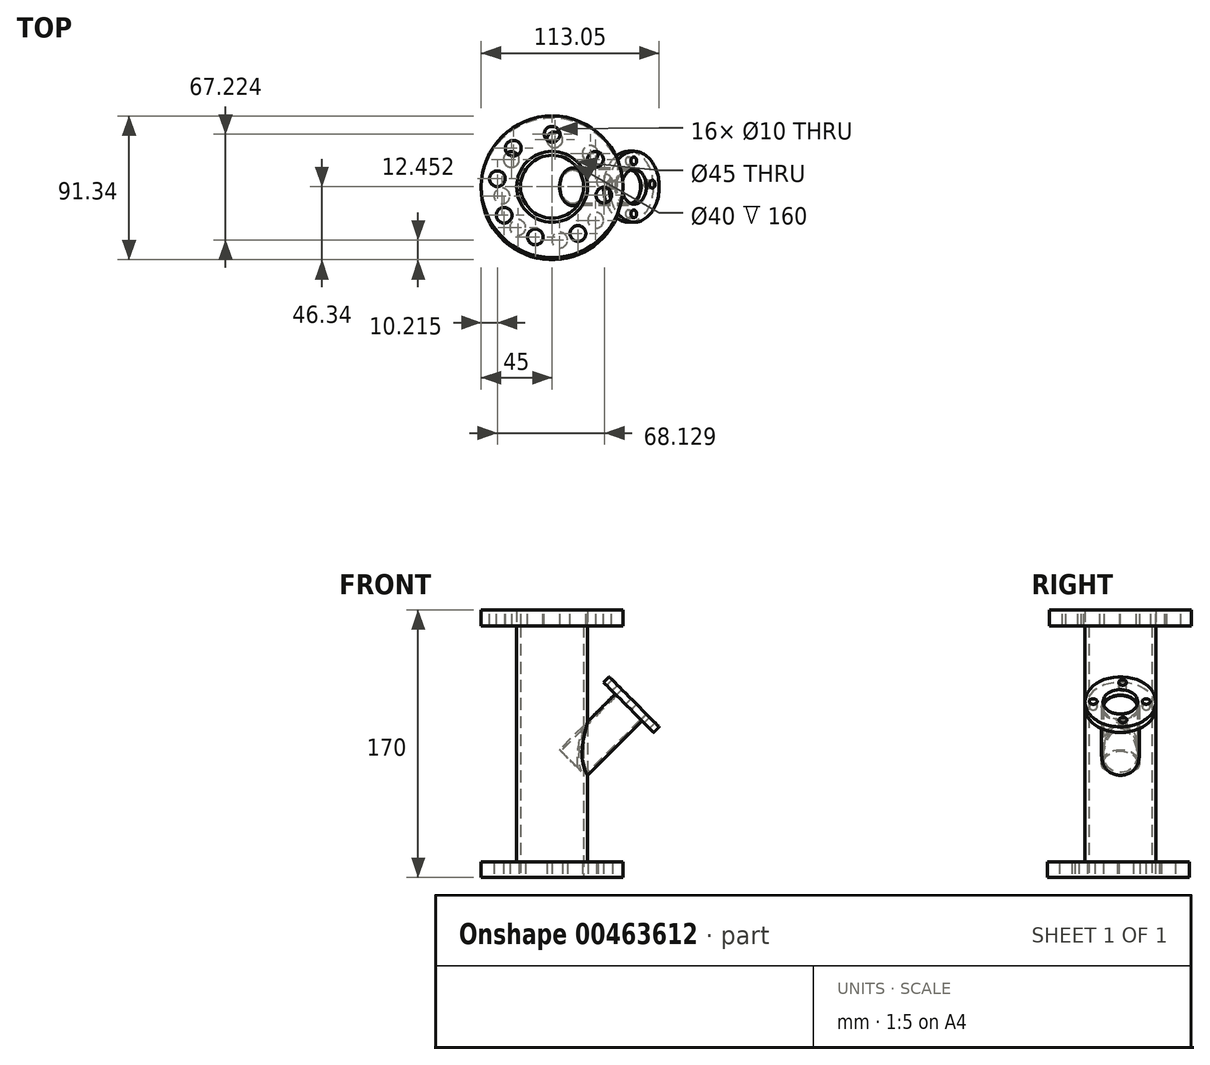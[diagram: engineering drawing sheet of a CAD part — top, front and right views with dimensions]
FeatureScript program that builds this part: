
annotation { "Feature Type Name" : "Feature", "Feature Type Description" : "" }
export const myFeature = defineFeature(function(context is Context, id is Id, definition is map)
    precondition{}
    {
        {
            var Q0;
            Q0=qCreatedBy(makeId("Top.planeOp"),FACE);
            var sketch = newSketch(context, id + "F0", { "sketchPlane" : qUnion([Q0])});
            skCircle(sketch, "E0", {"center": v(0, 0) * mm, "radius": 20 * mm});
            skCircle(sketch, "E1", {"center": v(0, 0) * mm, "radius": 22.5 * mm});
            skSolve(sketch);
        }
        {
            var Q0;
            Q0 = qSketchRegion(id + "F0", true);
            var Q1;
            Q1 = qSketchRegion(id + "F2", true);
            extrude(context, id + "F1", {"entities" : qUnion([Q0, Q1]), "depth" : 160 * mm});
        }
        {
            var Q0;
            Q0=qCreatedBy(makeId("Top.planeOp"),FACE);
            var sketch = newSketch(context, id + "F2", { "sketchPlane" : qUnion([Q0])});
            skCircle(sketch, "E2", {"center": v(0, -1.34) * mm, "radius": 45 * mm});
            skCircle(sketch, "E3", {"center": v(0, 0) * mm, "radius": 22.5 * mm});
            skSolve(sketch);
        }
        {
            var Q0;
            Q0=makeQuery(id+"F1.opExtrude","CAP_FACE",FACE,{"disambiguationData":[OSD([sQuery(id+"F0.wireOp",EDGE,"E0"),sQuery(id+"F0.wireOp",EDGE,"E1")])],"isStart":false});
            var sketch = newSketch(context, id + "F3", { "sketchPlane" : qUnion([Q0])});
            skCircle(sketch, "E4", {"center": v(0, 0) * mm, "radius": 45 * mm});
            skCircle(sketch, "E5", {"center": v(0, 0) * mm, "radius": 35 * mm, "construction": true});
            skSolve(sketch);
        }
        {
            var Q0;
            Q0=makeQuery(id+"F3.imprint","IMPRINT",FACE,{"disambiguationData":[TD([[makeQuery(id+"F3.imprint","IMPRINT",EDGE,{"derivedFrom":sQuery(id+"F3.wireOp",EDGE,"E4")}),1.0]])]});
            var Q1;
            Q1=sQuery(id+"F3.wireOp",EDGE,"E5");
            extrude(context, id + "F4", {"entities" : qUnion([Q0]), "surfaceEntities" : qUnion([Q1]), "depth" : 10 * mm});
        }
        {
            var Q0;
            Q0 = qSketchRegion(id + "F2", true);
            extrude(context, id + "F5", {"entities" : qUnion([Q0]), "operationType" : NewBodyOperationType.ADD, "depth" : 10 * mm});
        }
        {
            var Q0;
            Q0=qCreatedBy(makeId("Front.planeOp"),FACE);
            var sketch = newSketch(context, id + "F6", { "sketchPlane" : qUnion([Q0])});
            skLineSegment(sketch, "E6", {"start": v(0, 0) * mm, "end": v(0, 40) * mm});
            skLineSegment(sketch, "E7", {"start": v(0, 40) * mm, "end": v(23, 63) * mm});
            skLineSegment(sketch, "E8", {"start": v(23, 63) * mm, "end": v(3.42, 82.59) * mm});
            skSolve(sketch);
        }
        {
            var Q0;
            Q0=qCreatedBy(makeId("Right.planeOp"),FACE);
            var Q1;
            Q1=sQuery(id+"F6.wireOp",EDGE,"E8");
            cPlane(context, id + "F7", {"entities" : qUnion([Q0, Q1]), "cplaneType" : CPlaneType.LINE_ANGLE, "offset" : 25 * mm, "angle" : 0 * degree, "width" : 150 * mm, "height" : 150 * mm});
        }
        {
            var Q0;
            Q0=qCreatedBy(id+"F7.planeOp",FACE);
            var sketch = newSketch(context, id + "F8", { "sketchPlane" : qUnion([Q0])});
            skCircle(sketch, "E9", {"center": v(0, 42.08) * mm, "radius": 10.75 * mm});
            skCircle(sketch, "E10", {"center": v(0, 42.08) * mm, "radius": 12 * mm});
            skSolve(sketch);
        }
        {
            var Q0;
            Q0 = qSketchRegion(id + "F8", true);
            extrude(context, id + "F9", {"entities" : qUnion([Q0]), "operationType" : NewBodyOperationType.ADD, "oppositeDirection" : true, "depth" : 50 * mm});
        }
        {
            var Q0;
            Q0=makeQuery(id+"F9.opExtrude","CAP_FACE",FACE,{"disambiguationData":[OSD([sQuery(id+"F8.wireOp",EDGE,"E9"),sQuery(id+"F8.wireOp",EDGE,"E10")])],"isStart":false});
            var sketch = newSketch(context, id + "F10", { "sketchPlane" : qUnion([Q0])});
            skCircle(sketch, "E11", {"center": v(0, 42.08) * mm, "radius": 22.5 * mm});
            skCircle(sketch, "E12", {"center": v(0, 42.08) * mm, "radius": 11 * mm});
            skSolve(sketch);
        }
        {
            var Q0;
            Q0 = qSketchRegion(id + "F10", true);
            extrude(context, id + "F11", {"entities" : qUnion([Q0]), "operationType" : NewBodyOperationType.ADD, "depth" : 5 * mm});
        }
        {
            var Q0;
            Q0=makeQuery(id+"F4.opExtrude","CAP_FACE",FACE,{"disambiguationData":[OSD([sQuery(id+"F0.wireOp",EDGE,"E1"),sQuery(id+"F3.wireOp",EDGE,"E4")])],"isStart":false});
            var sketch = newSketch(context, id + "F12", { "sketchPlane" : qUnion([Q0])});
            skCircle(sketch, "E13", {"center": v(0, 33.34) * mm, "radius": 5 * mm});
            skCircle(sketch, "E14", {"center": v(-24.64, 24.4) * mm, "radius": 5 * mm});
            skCircle(sketch, "E15", {"center": v(-34.79, 5.07) * mm, "radius": 5 * mm});
            skCircle(sketch, "E16", {"center": v(-30.44, -18.12) * mm, "radius": 5 * mm});
            skCircle(sketch, "E17", {"center": v(-10.63, -31.89) * mm, "radius": 5 * mm});
            skCircle(sketch, "E18", {"center": v(16.43, -29.71) * mm, "radius": 5 * mm});
            skCircle(sketch, "E19", {"center": v(32.85, -5.31) * mm, "radius": 5 * mm});
            skCircle(sketch, "E20", {"center": v(27.54, 17.4) * mm, "radius": 5 * mm});
            skSolve(sketch);
        }
        {
            var Q0;
            Q0=makeQuery(id+"F12.imprint","IMPRINT",FACE,{"disambiguationData":[TD([[makeQuery(id+"F12.imprint","IMPRINT",EDGE,{"derivedFrom":sQuery(id+"F12.wireOp",EDGE,"E16")}),1.0]])]});
            var Q1;
            Q1=makeQuery(id+"F12.imprint","IMPRINT",FACE,{"disambiguationData":[TD([[makeQuery(id+"F12.imprint","IMPRINT",EDGE,{"derivedFrom":sQuery(id+"F12.wireOp",EDGE,"E15")}),1.0]])]});
            var Q2;
            Q2=makeQuery(id+"F12.imprint","IMPRINT",FACE,{"disambiguationData":[TD([[makeQuery(id+"F12.imprint","IMPRINT",EDGE,{"derivedFrom":sQuery(id+"F12.wireOp",EDGE,"E17")}),1.0]])]});
            var Q3;
            Q3=makeQuery(id+"F12.imprint","IMPRINT",FACE,{"disambiguationData":[TD([[makeQuery(id+"F12.imprint","IMPRINT",EDGE,{"derivedFrom":sQuery(id+"F12.wireOp",EDGE,"E18")}),1.0]])]});
            var Q4;
            Q4=makeQuery(id+"F12.imprint","IMPRINT",FACE,{"disambiguationData":[TD([[makeQuery(id+"F12.imprint","IMPRINT",EDGE,{"derivedFrom":sQuery(id+"F12.wireOp",EDGE,"E19")}),1.0]])]});
            var Q5;
            Q5=makeQuery(id+"F12.imprint","IMPRINT",FACE,{"disambiguationData":[TD([[makeQuery(id+"F12.imprint","IMPRINT",EDGE,{"derivedFrom":sQuery(id+"F12.wireOp",EDGE,"E20")}),1.0]])]});
            var Q6;
            Q6=makeQuery(id+"F12.imprint","IMPRINT",FACE,{"disambiguationData":[TD([[makeQuery(id+"F12.imprint","IMPRINT",EDGE,{"derivedFrom":sQuery(id+"F12.wireOp",EDGE,"E13")}),1.0]])]});
            var Q7;
            Q7=makeQuery(id+"F12.imprint","IMPRINT",FACE,{"disambiguationData":[TD([[makeQuery(id+"F12.imprint","IMPRINT",EDGE,{"derivedFrom":sQuery(id+"F12.wireOp",EDGE,"E14")}),1.0]])]});
            extrude(context, id + "F13", {"entities" : qUnion([Q0, Q1, Q2, Q3, Q4, Q5, Q6, Q7]), "operationType" : NewBodyOperationType.REMOVE, "oppositeDirection" : true, "depth" : 10 * mm});
        }
        {
            var Q0;
            Q0=makeQuery(id+"F11.opExtrude","CAP_FACE",FACE,{"disambiguationData":[OSD([sQuery(id+"F10.wireOp",EDGE,"E11"),sQuery(id+"F10.wireOp",EDGE,"E12")])],"isStart":false});
            var sketch = newSketch(context, id + "F14", { "sketchPlane" : qUnion([Q0])});
            skCircle(sketch, "E21", {"center": v(16.4, 42.4) * mm, "radius": 2.5 * mm});
            skCircle(sketch, "E22", {"center": v(-17.25, 42.37) * mm, "radius": 2.5 * mm});
            skCircle(sketch, "E23", {"center": v(1.4, 59.47) * mm, "radius": 2.5 * mm});
            skCircle(sketch, "E24", {"center": v(1.64, 25.77) * mm, "radius": 2.5 * mm});
            skSolve(sketch);
        }
        {
            var Q0;
            Q0 = qSketchRegion(id + "F14", true);
            extrude(context, id + "F15", {"entities" : qUnion([Q0]), "operationType" : NewBodyOperationType.REMOVE, "oppositeDirection" : true, "depth" : 5 * mm});
        }
        {
            var Q0;
            Q0=makeQuery(id+"F5.boolean.opBoolean","MERGE",FACE,{"derivedFrom":[makeQuery(id+"F1.opExtrude","CAP_FACE",FACE,{"disambiguationData":[OSD([sQuery(id+"F0.wireOp",EDGE,"E0"),sQuery(id+"F0.wireOp",EDGE,"E1")])],"isStart":true}),makeQuery(id+"F5.opExtrude","CAP_FACE",FACE,{"disambiguationData":[OSD([sQuery(id+"F2.wireOp",EDGE,"E2"),sQuery(id+"F2.wireOp",EDGE,"E3")])],"isStart":true})]});
            var sketch = newSketch(context, id + "F16", { "sketchPlane" : qUnion([Q0])});
            skCircle(sketch, "E25", {"center": v(1.7, -29.86) * mm, "radius": 5 * mm});
            skCircle(sketch, "E26", {"center": v(24.26, -21.1) * mm, "radius": 5 * mm});
            skCircle(sketch, "E27", {"center": v(33.34, -3.08) * mm, "radius": 5 * mm});
            skCircle(sketch, "E28", {"center": v(27.7, 21.36) * mm, "radius": 5 * mm});
            skCircle(sketch, "E29", {"center": v(4.84, 33.89) * mm, "radius": 5 * mm});
            skCircle(sketch, "E30", {"center": v(-21.8, 25.9) * mm, "radius": 5 * mm});
            skCircle(sketch, "E31", {"center": v(-31.82, 5.85) * mm, "radius": 5 * mm});
            skCircle(sketch, "E32", {"center": v(-25.86, -17.33) * mm, "radius": 5 * mm});
            skSolve(sketch);
        }
        {
            var Q0;
            Q0 = qSketchRegion(id + "F16", true);
            extrude(context, id + "F17", {"entities" : qUnion([Q0]), "operationType" : NewBodyOperationType.REMOVE, "oppositeDirection" : true, "depth" : 10 * mm});
        }
    });
